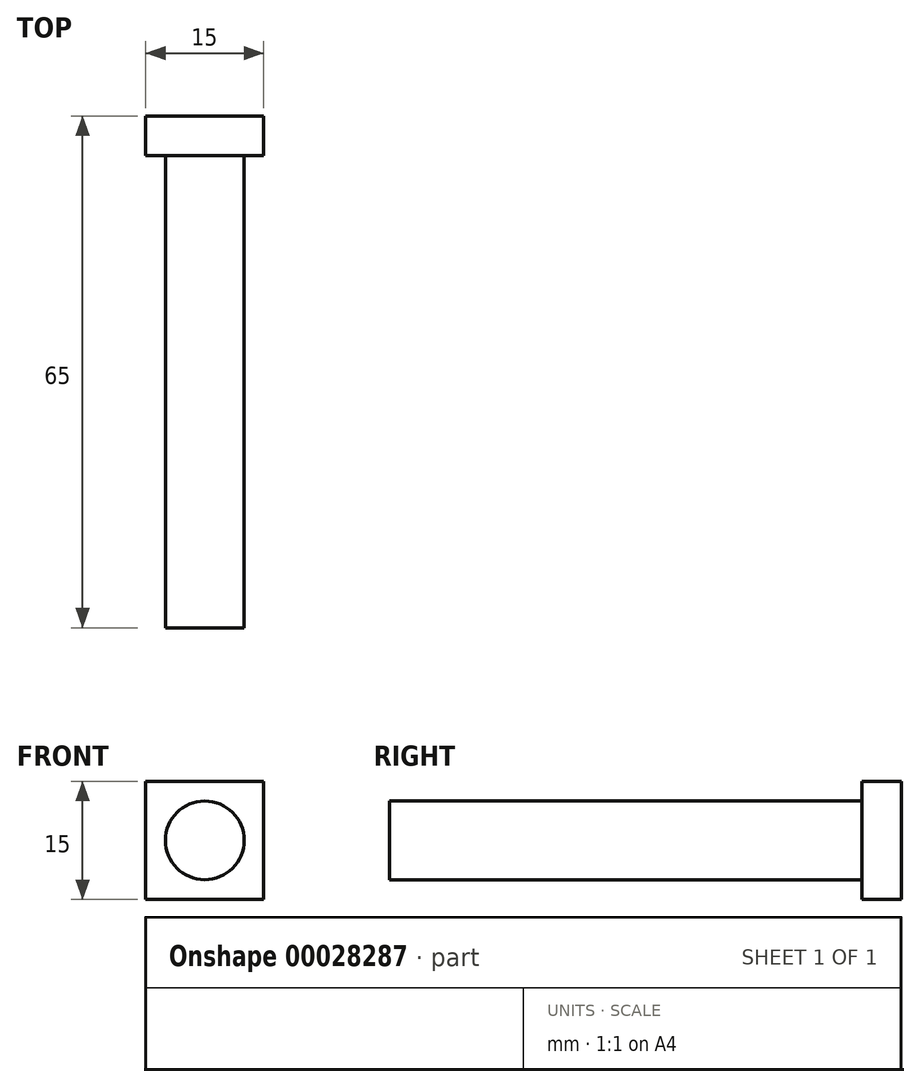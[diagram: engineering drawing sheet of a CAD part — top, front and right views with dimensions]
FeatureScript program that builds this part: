
annotation { "Feature Type Name" : "Feature", "Feature Type Description" : "" }
export const myFeature = defineFeature(function(context is Context, id is Id, definition is map)
    precondition{}
    {
        {
            var Q0;
            Q0=qCreatedBy(makeId("Front.planeOp"),FACE);
            var sketch = newSketch(context, id + "F0", { "sketchPlane" : qUnion([Q0])});
            skCircle(sketch, "E0", {"center": v(0, 0) * mm, "radius": 5 * mm});
            skSolve(sketch);
        }
        {
            var Q0;
            Q0=makeQuery(id+"F0.imprint","IMPRINT",FACE,{"disambiguationData":[TD([[makeQuery(id+"F0.imprint","IMPRINT",EDGE,{"derivedFrom":sQuery(id+"F0.wireOp",EDGE,"E0")}),1.0]])]});
            extrude(context, id + "F1", {"entities" : qUnion([Q0]), "depth" : 60 * mm});
        }
        {
            var Q0;
            Q0=makeQuery(id+"F1.opExtrude","CAP_FACE",FACE,{"disambiguationData":[OSD([sQuery(id+"F0.wireOp",EDGE,"E0")])],"isStart":true});
            var sketch = newSketch(context, id + "F2", { "sketchPlane" : qUnion([Q0])});
            skLineSegment(sketch, "E1.rect.bottom", {"start": v(7.5, -7.5) * mm, "end": v(-7.5, -7.5) * mm});
            skLineSegment(sketch, "E1.rect.top", {"start": v(7.5, 7.5) * mm, "end": v(-7.5, 7.5) * mm});
            skLineSegment(sketch, "E1.rect.left", {"start": v(7.5, -7.5) * mm, "end": v(7.5, 7.5) * mm});
            skLineSegment(sketch, "E1.rect.right", {"start": v(-7.5, -7.5) * mm, "end": v(-7.5, 7.5) * mm});
            skPoint(sketch, "E1.rect.middle", {"position": v(0, 0) * mm});
            skSolve(sketch);
        }
        {
            var Q0;
            Q0=qSketchRegion(id+"F2",true);
            extrude(context, id + "F3", {"entities" : qUnion([Q0]), "operationType" : NewBodyOperationType.ADD, "depth" : 5 * mm});
        }
    });
